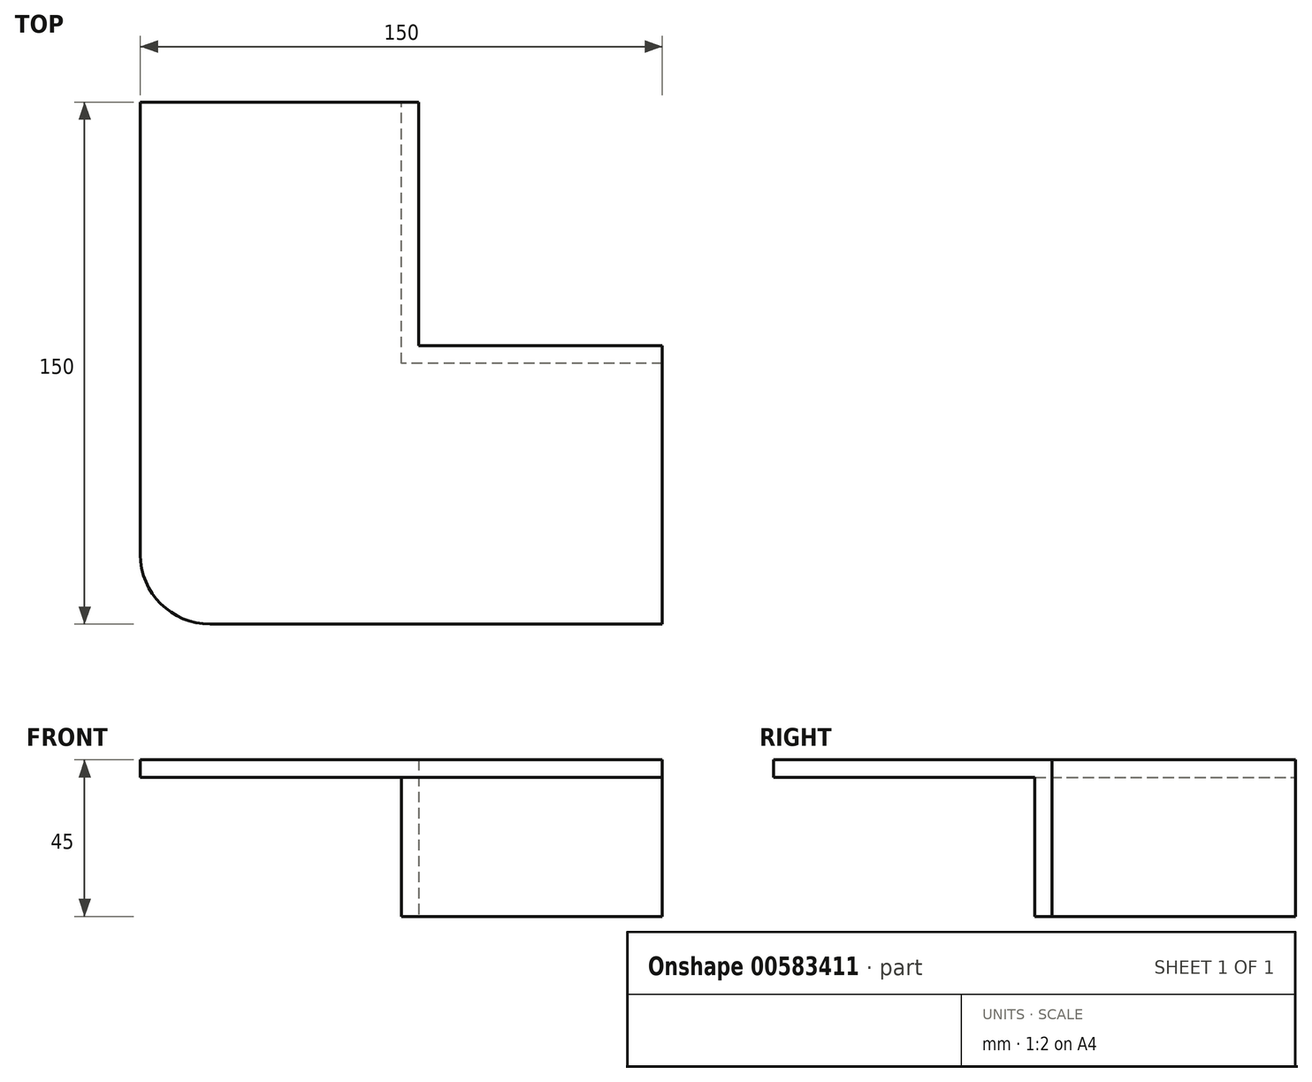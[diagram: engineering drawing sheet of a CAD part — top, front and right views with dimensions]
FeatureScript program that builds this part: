
annotation { "Feature Type Name" : "Feature", "Feature Type Description" : "" }
export const myFeature = defineFeature(function(context is Context, id is Id, definition is map)
    precondition{}
    {
        {
            var Q0;
            Q0=qCreatedBy(makeId("Top.planeOp"),FACE);
            var sketch = newSketch(context, id + "F0", { "sketchPlane" : qUnion([Q0])});
            skLineSegment(sketch, "E0.bottom", {"start": v(20, 0) * mm, "end": v(150, 0) * mm});
            skLineSegment(sketch, "E0.top", {"start": v(80, 80) * mm, "end": v(150, 80) * mm});
            skLineSegment(sketch, "E0.right", {"start": v(150, 0) * mm, "end": v(150, 80) * mm});
            skLineSegment(sketch, "E1.top", {"start": v(0, 150) * mm, "end": v(80, 150) * mm});
            skLineSegment(sketch, "E1.left", {"start": v(0, 20) * mm, "end": v(0, 150) * mm});
            skLineSegment(sketch, "E1.right", {"start": v(80, 80) * mm, "end": v(80, 150) * mm});
            skPoint(sketch, "E2.visualSharp", {"position": v(0, 0) * mm});
            skArc(sketch, "E2.filletArc", {"start": v(0, 20) * mm, "mid": v(5.86, 5.86) * mm, "end": v(20, 0) * mm});
            skSolve(sketch);
        }
        {
            var Q0;
            Q0=makeQuery(id+"F0.imprint","IMPRINT",FACE,{"disambiguationData":[TD([[makeQuery(id+"F0.imprint","IMPRINT",EDGE,{"derivedFrom":sQuery(id+"F0.wireOp",EDGE,"E0.bottom")}),1.0]])]});
            extrude(context, id + "F1", {"entities" : qUnion([Q0]), "depth" : 5 * mm, "offsetDistance" : 25 * mm});
        }
        {
            var Q0;
            Q0=makeQuery(id+"F1.opExtrude","CAP_FACE",FACE,{"disambiguationData":[OSD([sQuery(id+"F0.wireOp",EDGE,"E0.bottom"),sQuery(id+"F0.wireOp",EDGE,"E0.top"),sQuery(id+"F0.wireOp",EDGE,"E0.right"),sQuery(id+"F0.wireOp",EDGE,"E1.top"),sQuery(id+"F0.wireOp",EDGE,"E1.left"),sQuery(id+"F0.wireOp",EDGE,"E1.right"),sQuery(id+"F0.wireOp",EDGE,"E2.filletArc")])],"isStart":true});
            var sketch = newSketch(context, id + "F2", { "sketchPlane" : qUnion([Q0])});
            skLineSegment(sketch, "E3.bottom", {"start": v(150, -80) * mm, "end": v(80, -80) * mm});
            skLineSegment(sketch, "E3.top", {"start": v(150, -75) * mm, "end": v(75, -75) * mm});
            skLineSegment(sketch, "E3.left", {"start": v(150, -80) * mm, "end": v(150, -75) * mm});
            skLineSegment(sketch, "E4.top", {"start": v(75, -150) * mm, "end": v(80, -150) * mm});
            skLineSegment(sketch, "E4.left", {"start": v(75, -75) * mm, "end": v(75, -150) * mm});
            skLineSegment(sketch, "E4.right", {"start": v(80, -80) * mm, "end": v(80, -150) * mm});
            skSolve(sketch);
        }
        {
            var Q0;
            Q0=makeQuery(id+"F2.imprint","IMPRINT",FACE,{"disambiguationData":[TD([[makeQuery(id+"F2.imprint","IMPRINT",EDGE,{"derivedFrom":sQuery(id+"F2.wireOp",EDGE,"E3.bottom")}),1.0]])]});
            extrude(context, id + "F3", {"entities" : qUnion([Q0]), "operationType" : NewBodyOperationType.ADD, "depth" : 40 * mm, "offsetDistance" : 25 * mm});
        }
    });
